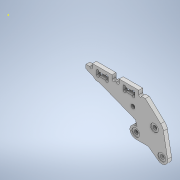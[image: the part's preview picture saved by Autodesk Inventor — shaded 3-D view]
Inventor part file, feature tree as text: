
AUTODESK INVENTOR PART (.ipt)
format: ipt  version: 2020.2 (Build 242310000, 310)  size: 406,016 bytes
history: native  units: mm
features: sketch x5, extrude x3, other x2, hole x2, projected_geometry x1
ambient origin geometry x8: Origin, YZ Plane, XZ Plane, XY Plane, X Axis, Y Axis, Z Axis, Center Point
bodies: Body1 (feature_tree)
feature tree (13):
  other  "ソリッド1"
  sketch  "スケッチ2"
  sketch  "スケッチ1"
  extrude  "押し出し1"  Depth=9.0mm
  hole  "穴1"  [1 undecoded]
  extrude  "押し出し2"  Depth=9.0mm
  hole  "穴2"  [1 undecoded]
  sketch  "スケッチ4"
  extrude  "押し出し3"  Depth=8.0mm
  sketch  "スケッチ6"
  sketch  "スケッチ5"
  projected_geometry  "投影ループ1"
  other  "断面エッジを投影1"
note: 2 required parameter values undecoded (feature->parameter linkage not recoverable at this tier; creation-order binding heuristic only, values carry confidence <= 0.55)
